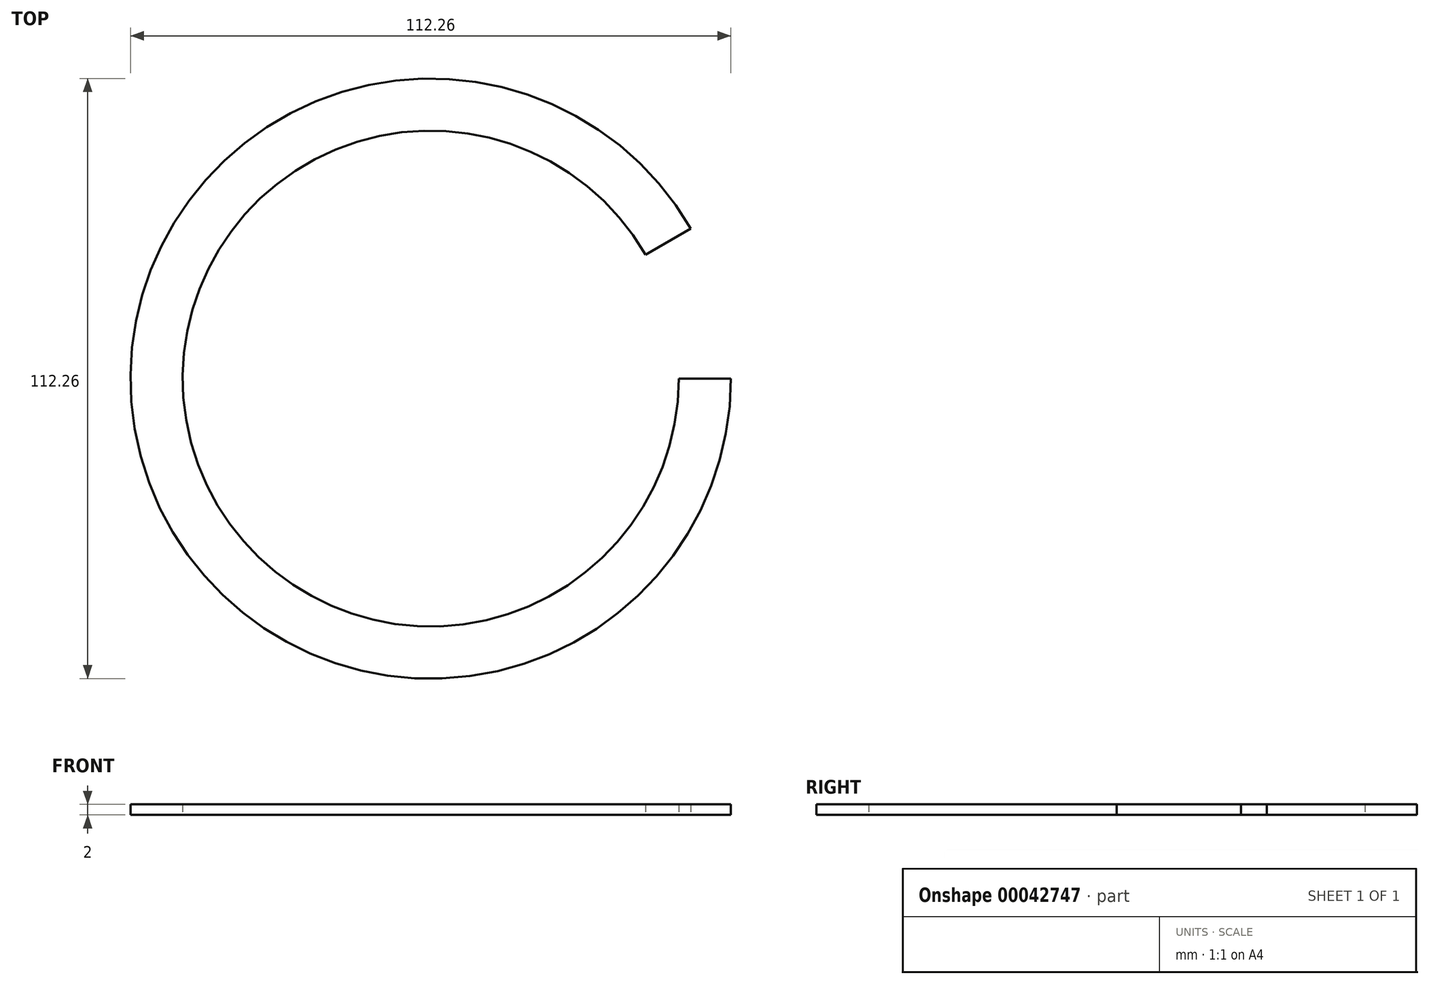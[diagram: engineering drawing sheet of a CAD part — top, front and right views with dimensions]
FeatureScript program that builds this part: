
annotation { "Feature Type Name" : "Feature", "Feature Type Description" : "" }
export const myFeature = defineFeature(function(context is Context, id is Id, definition is map)
    precondition{}
    {
        {
            var Q0;
            Q0=qCreatedBy(makeId("Top.planeOp"),FACE);
            var sketch = newSketch(context, id + "F0", { "sketchPlane" : qUnion([Q0])});
            skArc(sketch, "E0", {"start": v(48.6, 28.06) * mm, "mid": v(-54.22, -14.53) * mm, "end": v(56.13, 0) * mm});
            skArc(sketch, "E1", {"start": v(40.16, 23.19) * mm, "mid": v(-44.8, -12) * mm, "end": v(46.37, 0) * mm});
            skLineSegment(sketch, "E2", {"start": v(56.13, 0) * mm, "end": v(46.37, 0) * mm});
            skLineSegment(sketch, "E3", {"start": v(40.16, 23.19) * mm, "end": v(48.6, 28.06) * mm});
            skSolve(sketch);
        }
        {
            var Q0;
            Q0 = qSketchRegion(id + "F0", true);
            extrude(context, id + "F1", {"entities" : qUnion([Q0]), "depth" : 2 * mm});
        }
    });
